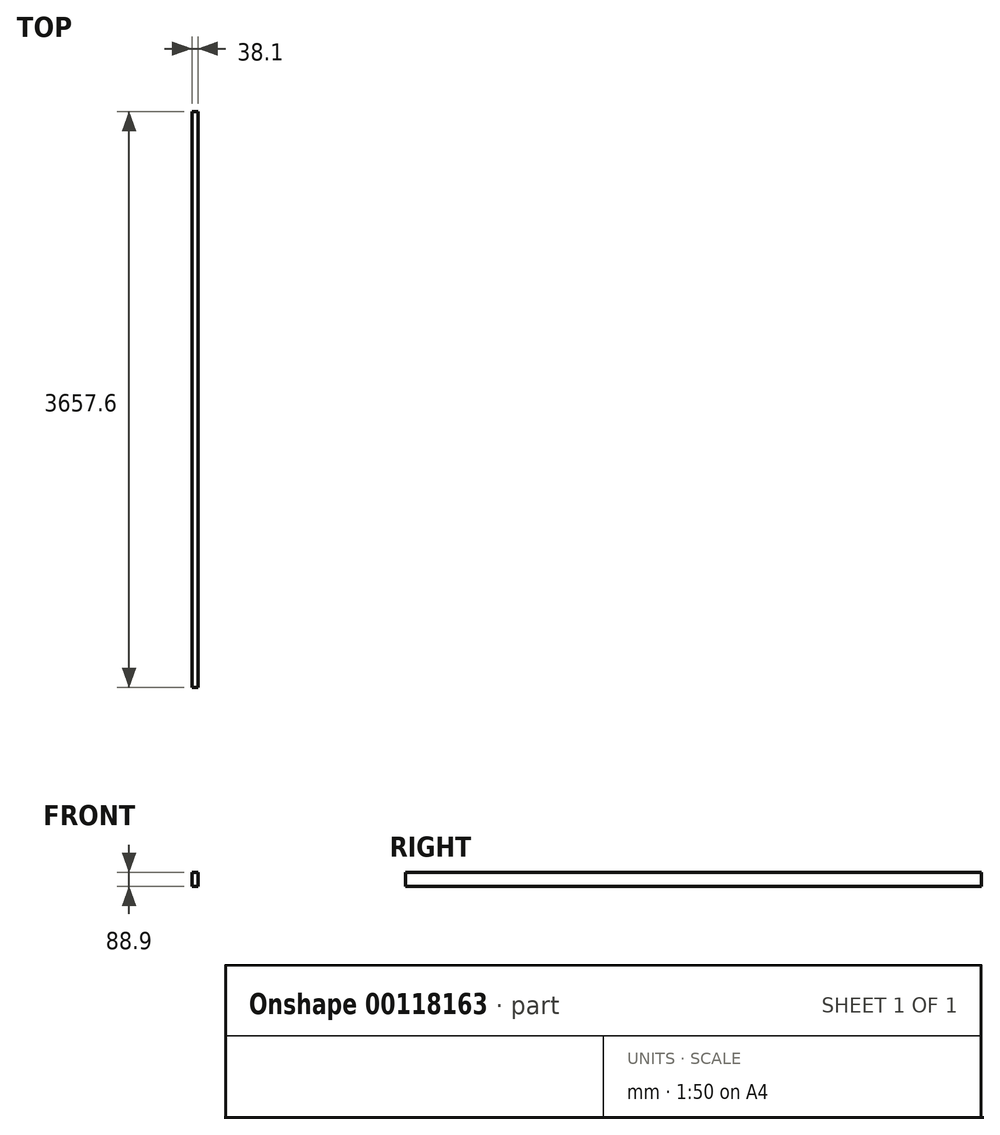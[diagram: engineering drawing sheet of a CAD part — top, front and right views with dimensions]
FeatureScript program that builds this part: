
annotation { "Feature Type Name" : "Feature", "Feature Type Description" : "" }
export const myFeature = defineFeature(function(context is Context, id is Id, definition is map)
    precondition{}
    {
        {
            var Q0;
            Q0=qCreatedBy(makeId("Front.planeOp"),FACE);
            var sketch = newSketch(context, id + "F0", { "sketchPlane" : qUnion([Q0])});
            skLineSegment(sketch, "E0.bottom", {"start": v(0, 0) * mm, "end": v(38.1, 0) * mm});
            skLineSegment(sketch, "E0.top", {"start": v(0, 88.9) * mm, "end": v(38.1, 88.9) * mm});
            skLineSegment(sketch, "E0.left", {"start": v(0, 0) * mm, "end": v(0, 88.9) * mm});
            skLineSegment(sketch, "E0.right", {"start": v(38.1, 0) * mm, "end": v(38.1, 88.9) * mm});
            skSolve(sketch);
        }
        {
            var Q0;
            Q0 = qSketchRegion(id + "F0", true);
            extrude(context, id + "F1", {"entities" : qUnion([Q0]), "depth" : 3657.6 * mm});
        }
    });
